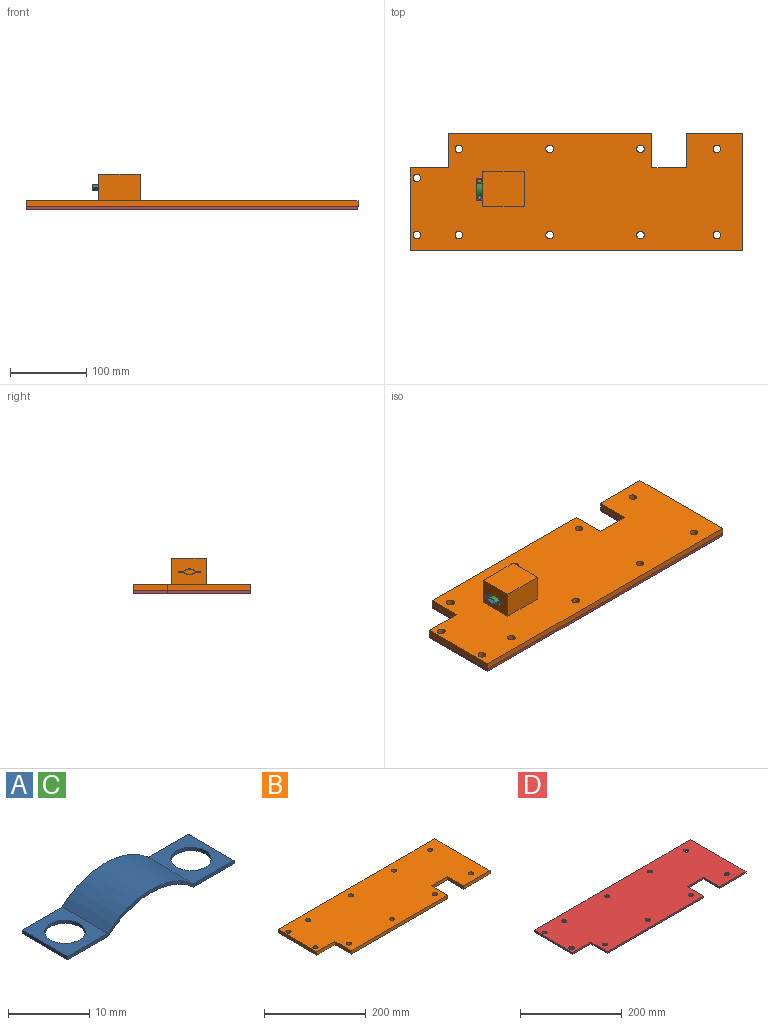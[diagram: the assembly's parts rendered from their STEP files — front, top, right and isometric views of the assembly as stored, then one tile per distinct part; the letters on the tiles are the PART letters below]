
ASSEMBLY  parts=4 mates=3
PART A: 12 faces, bbox 29x8x3.4 mm
  f0: cylinder r=11.23mm len=15mm, axis (0,1,0), area 131.4mm2, adj f1,f7,f8,f9
  f1: plane 8x7mm, normal (0,0,-1), area 36.4mm2, adj f0,f2,f8,f9,f11
  f2: plane 8x0.5mm, normal (1,0,0), area 4mm2, adj f1,f3,f8,f9
  f3: plane 8x7mm, normal (0,0,1), area 36.4mm2, adj f2,f4,f8,f9,f11
  f4: cylinder r=11.23mm len=15mm, axis (0,1,0), area 131.4mm2, adj f3,f5,f8,f9
  f5: plane 8x7mm, normal (0,0,1), area 36.4mm2, adj f4,f6,f8,f9,f10
  f6: plane 8x0.5mm, normal (-1,0,0), area 4mm2, adj f5,f7,f8,f9
  f7: plane 8x7mm, normal (0,0,-1), area 36.4mm2, adj f0,f6,f8,f9,f10
  f8: plane 29x3.37mm, normal (0,-1,0), area 14.5mm2, adj f0,f1,f2,f3,f4,f5,f6,f7
  f9: plane 29x3.37mm, normal (0,1,0), area 14.5mm2, adj f0,f1,f2,f3,f4,f5,f6,f7
  f10: cylinder r=2.5mm len=5mm, axis (0,0,1), area 7.9mm2, adj f5,f7
  f11: cylinder r=2.5mm len=5mm, axis (0,0,1), area 7.9mm2, adj f1,f3
PART B: 27 faces, bbox 435x153x43 mm
  f0: plane 435x153mm, normal (0,0,-1), area 59019.6mm2, adj f1,f2,f3,f5,f6,f7,f8,f9
  f1: plane 108x8mm, normal (-1,0,0), area 864mm2, adj f0,f4,f6,f20
  f2: plane 73x8mm, normal (0,-1,0), area 584mm2, adj f0,f4,f5,f17
  f3: plane 267x8mm, normal (0,-1,0), area 2136mm2, adj f0,f4,f19,f21
  f4: plane 435x153mm, normal (0,0,1), area 61494.6mm2, adj f1,f2,f3,f5,f6,f7,f8,f9
  f5: plane 153x8mm, normal (1,0,0), area 1224mm2, adj f0,f2,f4,f6
  f6: plane 435x8mm, normal (0,1,0), area 3480mm2, adj f0,f1,f4,f5
  f7: cylinder r=5mm len=10mm, axis (0,0,1), area 251.3mm2, adj f0,f4
  f8: cylinder r=5mm len=10mm, axis (0,0,1), area 251.3mm2, adj f0,f4
  f9: cylinder r=5mm len=10mm, axis (0,0,1), area 251.3mm2, adj f0,f4
  f10: cylinder r=5mm len=10mm, axis (0,0,1), area 251.3mm2, adj f0,f4
  f11: cylinder r=5mm len=10mm, axis (0,0,1), area 251.3mm2, adj f0,f4
  f12: cylinder r=5mm len=10mm, axis (0,0,1), area 251.3mm2, adj f0,f4
  f13: cylinder r=5mm len=10mm, axis (0,0,1), area 251.3mm2, adj f0,f4
  f14: cylinder r=5mm len=10mm, axis (0,0,1), area 251.3mm2, adj f0,f4
  f15: cylinder r=5mm len=10mm, axis (0,0,1), area 251.3mm2, adj f0,f4
  f16: cylinder r=5mm len=10mm, axis (0,0,1), area 251.3mm2, adj f0,f4
  f17: plane 45x8mm, normal (-1,0,0), area 360mm2, adj f0,f2,f4,f18
  f18: plane 45x8mm, normal (0,-1,0), area 360mm2, adj f0,f4,f17,f19
  f19: plane 45x8mm, normal (1,0,0), area 360mm2, adj f0,f3,f4,f18
  f20: plane 50x8mm, normal (0,-1,0), area 400mm2, adj f0,f1,f4,f21
  f21: plane 45x8mm, normal (-1,0,0), area 360mm2, adj f0,f3,f4,f20
  f22: plane 55x35mm, normal (0,1,0), area 1925mm2, adj f0,f23,f25,f26
  f23: plane 45x35mm, normal (-1,0,0), area 1575mm2, adj f0,f22,f24,f26
  f24: plane 55x35mm, normal (0,-1,0), area 1925mm2, adj f0,f23,f25,f26
  f25: plane 45x35mm, normal (1,0,0), area 1575mm2, adj f0,f22,f24,f26
  f26: plane 55x45mm, normal (0,0,-1), area 2475mm2, adj f22,f23,f24,f25
PART C: same geometry as A
PART D: 22 faces, bbox 435x153x4 mm
  f0: plane 108x4mm, normal (-1,0,0), area 432mm2, adj f3,f4,f6,f20
  f1: plane 73x4mm, normal (0,-1,0), area 292mm2, adj f3,f4,f5,f17
  f2: plane 267x4mm, normal (0,-1,0), area 1068mm2, adj f3,f4,f19,f21
  f3: plane 435x153mm, normal (0,0,1), area 61494.6mm2, adj f0,f1,f2,f5,f6,f7,f8,f9
  f4: plane 435x153mm, normal (0,0,-1), area 61494.6mm2, adj f0,f1,f2,f5,f6,f7,f8,f9
  f5: plane 153x4mm, normal (1,0,0), area 612mm2, adj f1,f3,f4,f6
  f6: plane 435x4mm, normal (0,1,0), area 1740mm2, adj f0,f3,f4,f5
  f7: cylinder r=5mm len=10mm, axis (0,0,1), area 125.7mm2, adj f3,f4
  f8: cylinder r=5mm len=10mm, axis (0,0,1), area 125.7mm2, adj f3,f4
  f9: cylinder r=5mm len=10mm, axis (0,0,1), area 125.7mm2, adj f3,f4
  f10: cylinder r=5mm len=10mm, axis (0,0,1), area 125.7mm2, adj f3,f4
  f11: cylinder r=5mm len=10mm, axis (0,0,1), area 125.7mm2, adj f3,f4
  f12: cylinder r=5mm len=10mm, axis (0,0,1), area 125.7mm2, adj f3,f4
  f13: cylinder r=5mm len=10mm, axis (0,0,1), area 125.7mm2, adj f3,f4
  f14: cylinder r=5mm len=10mm, axis (0,0,1), area 125.7mm2, adj f3,f4
  f15: cylinder r=5mm len=10mm, axis (0,0,1), area 125.7mm2, adj f3,f4
  f16: cylinder r=5mm len=10mm, axis (0,0,1), area 125.7mm2, adj f3,f4
  f17: plane 45x4mm, normal (-1,0,0), area 180mm2, adj f1,f3,f4,f18
  f18: plane 45x4mm, normal (0,-1,0), area 180mm2, adj f3,f4,f17,f19
  f19: plane 45x4mm, normal (1,0,0), area 180mm2, adj f2,f3,f4,f18
  f20: plane 50x4mm, normal (0,-1,0), area 200mm2, adj f0,f3,f4,f21
  f21: plane 45x4mm, normal (-1,0,0), area 180mm2, adj f2,f3,f4,f20
PLACE A rot(axis=(-0.71,-0.71,0),180deg) t=(277.13,33.39,-241.53)mm
PLACE B rot(axis=(-1,0,0),180deg) t=(182.13,126.4,-258.03)mm
PLACE C rot(axis=(0,0,1),90deg) t=(269.13,33.39,-240.53)mm
PLACE D rot(axis=(-1,0,0),180deg) t=(182.13,126.4,-266.03)mm
MATE fastened B.f4 <-> D.f4  axis (0,0,-1) through (402.98,33.68,-266.03)mm
MATE fastened C.f8 <-> B.f23  axis (1,0,0) through (277.13,33.39,-240.53)mm
MATE fastened A.f9 <-> B.f23  axis (1,0,0) through (277.13,33.39,-241.53)mm
